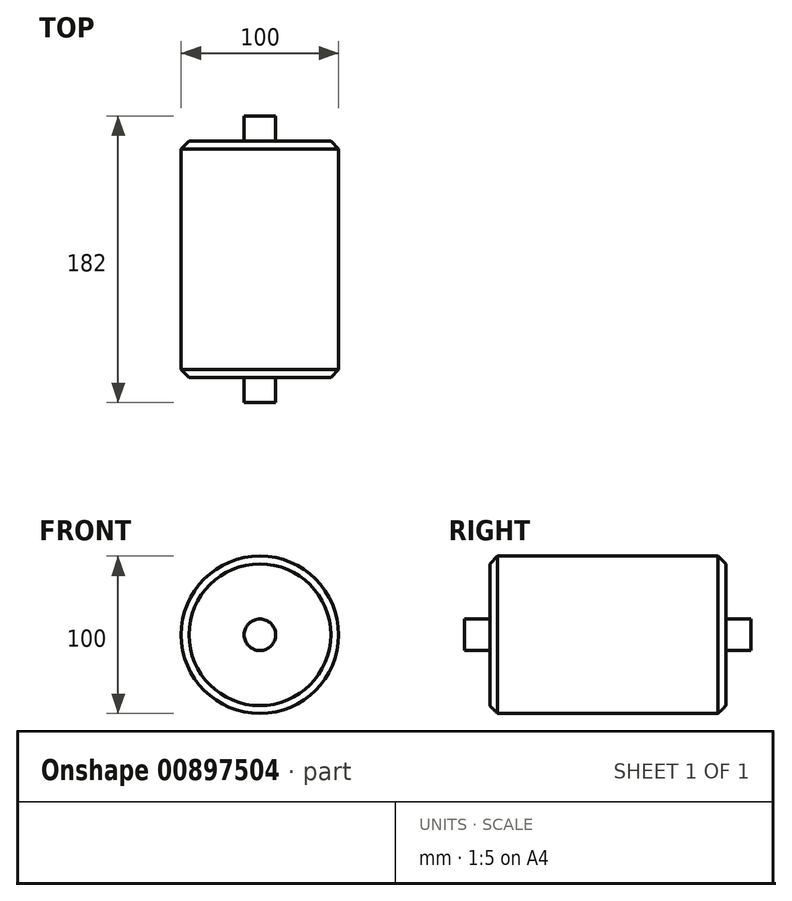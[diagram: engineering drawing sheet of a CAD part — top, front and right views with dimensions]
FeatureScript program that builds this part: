
annotation { "Feature Type Name" : "Feature", "Feature Type Description" : "" }
export const myFeature = defineFeature(function(context is Context, id is Id, definition is map)
    precondition{}
    {
        {
            var Q0;
            Q0=qCreatedBy(makeId("Front.planeOp"),FACE);
            var sketch = newSketch(context, id + "F0", { "sketchPlane" : qUnion([Q0])});
            skCircle(sketch, "E0", {"center": v(0, 0) * mm, "radius": 50 * mm});
            skSolve(sketch);
        }
        {
            var Q0;
            Q0 = qSketchRegion(id + "F0", true);
            extrude(context, id + "F1", {"entities" : qUnion([Q0]), "oppositeDirection" : true, "depth" : 150 * mm, "offsetDistance" : 25.4 * mm});
        }
        {
            var Q0;
            Q0=makeQuery(id+"F1.opExtrude","CAP_FACE",FACE,{"disambiguationData":[OSD([sQuery(id+"F0.wireOp",EDGE,"E0")])],"isStart":true});
            chamfer(context, id + "F2", {"entities" : qUnion([Q0]), "chamferType" : ChamferType.OFFSET_ANGLE, "width" : 5 * mm, "oppositeDirection" : false, "angle" : 45 * degree, "tangentPropagation" : true});
        }
        {
            var Q0;
            Q0=makeQuery(id+"F1.opExtrude","CAP_FACE",FACE,{"disambiguationData":[OSD([sQuery(id+"F0.wireOp",EDGE,"E0")])],"isStart":true});
            var sketch = newSketch(context, id + "F3", { "sketchPlane" : qUnion([Q0])});
            skCircle(sketch, "E1", {"center": v(0, 0) * mm, "radius": 10 * mm});
            skSolve(sketch);
        }
        {
            var Q0;
            Q0 = qSketchRegion(id + "F3", true);
            extrude(context, id + "F4", {"entities" : qUnion([Q0]), "operationType" : NewBodyOperationType.ADD, "depth" : 16 * mm, "offsetDistance" : 25.4 * mm});
        }
        {
            var Q0;
            Q0=makeQuery(id+"F1.opExtrude","CAP_FACE",FACE,{"disambiguationData":[OSD([sQuery(id+"F0.wireOp",EDGE,"E0")])],"isStart":false});
            chamfer(context, id + "F5", {"entities" : qUnion([Q0]), "chamferType" : ChamferType.OFFSET_ANGLE, "width" : 5 * mm, "oppositeDirection" : false, "angle" : 45 * degree, "tangentPropagation" : true});
        }
        {
            var Q0;
            Q0=makeQuery(id+"F1.opExtrude","CAP_FACE",FACE,{"disambiguationData":[OSD([sQuery(id+"F0.wireOp",EDGE,"E0")])],"isStart":false});
            var sketch = newSketch(context, id + "F6", { "sketchPlane" : qUnion([Q0])});
            skCircle(sketch, "E2", {"center": v(0, 0) * mm, "radius": 10 * mm});
            skSolve(sketch);
        }
        {
            var Q0;
            Q0 = qSketchRegion(id + "F6", true);
            extrude(context, id + "F7", {"entities" : qUnion([Q0]), "operationType" : NewBodyOperationType.ADD, "depth" : 16 * mm, "offsetDistance" : 25.4 * mm});
        }
    });
